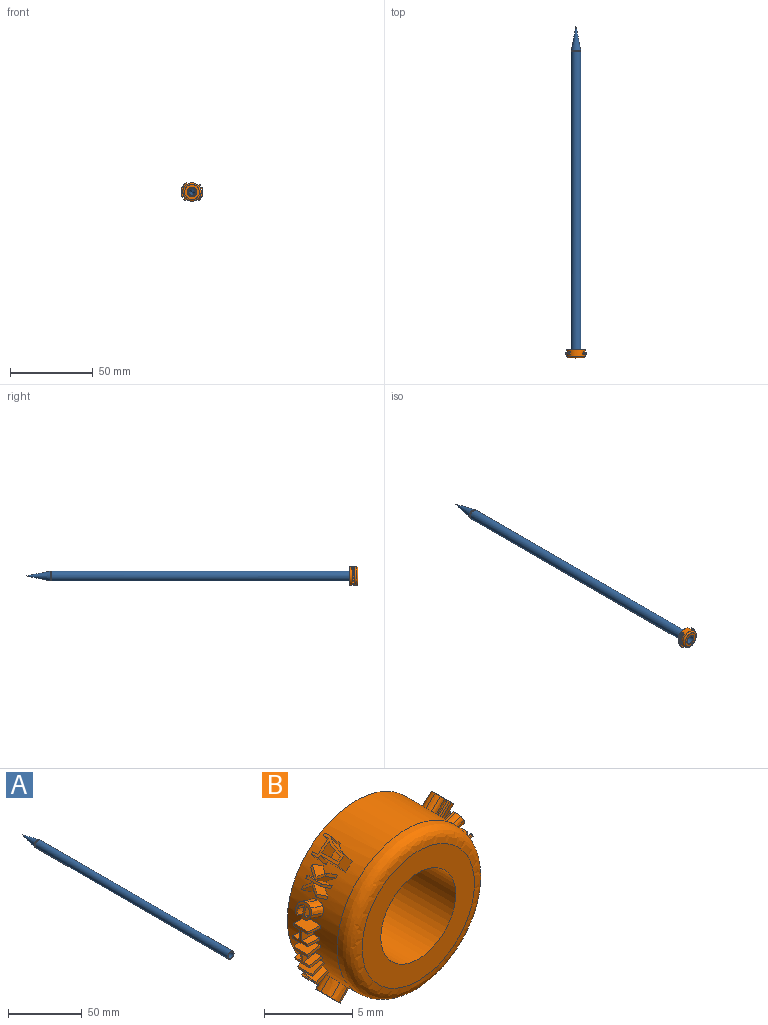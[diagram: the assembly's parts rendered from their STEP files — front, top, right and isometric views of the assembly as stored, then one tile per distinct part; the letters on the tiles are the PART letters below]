
ASSEMBLY  parts=2 mates=1
PART A: 8 faces, bbox 6x200x6 mm
  f0: cylinder r=2.5mm len=185mm, axis (0,1,0), area 2906mm2, adj f2,f4
  f1: cylinder r=3mm len=184.51mm, axis (0,1,0), area 3477.8mm2, adj f2,f5
  f2: plane 6x6mm, normal (0,-1,0), area 8.6mm2, adj f0,f1
  f3: cone r=3mm half-angle=11.3deg, axis (0,-1,0), area 135mm2, adj f5
  f4: plane 5x5mm, normal (0,-1,0), area 7.5mm2, adj f0,f6
  f5: revolved ~6x6mm, area 18.4mm2, adj f1,f3
  f6: revolved ~3.94x3.94mm, area 3.6mm2, adj f4,f7
  f7: cone r=2.02mm half-angle=11.3deg, axis (0,-1,0), area 59.2mm2, adj f6
PART B: 292 faces, bbox 13x5x11.3 mm
  f0: plane 1.56x0.74mm, normal (0.74,0,0.67), area 1.6mm2, adj f1,f9,f10,f32
  f1: plane 0.87x0.8mm, normal (0,-1,0), area 0.2mm2, adj f0,f2,f10,f32
  f2: plane 1.57x0.74mm, normal (-0.74,0,-0.67), area 1.6mm2, adj f1,f3,f10,f32
  f3: extruded ~0.78x0.71mm, area 0.2mm2, adj f2,f4,f10,f32
  f4: extruded ~0.86x0.79mm, area 0.2mm2, adj f3,f5,f10,f32
  f5: extruded ~0.86x0.79mm, area 0.2mm2, adj f4,f6,f10,f32
  f6: plane 0.75x0.67mm, normal (-0.74,0,-0.67), area 0.2mm2, adj f5,f7,f10,f32
  f7: extruded ~0.86x0.79mm, area 0.2mm2, adj f6,f8,f10,f32
  f8: extruded ~0.95x0.89mm, area 0.3mm2, adj f7,f9,f10,f32
  f9: extruded ~0.81x0.75mm, area 0.3mm2, adj f0,f8,f10,f32
  f10: cylinder r=6.5mm len=1.99mm, axis (0,1,0), area 0.4mm2, adj f0,f1,f2,f3,f4,f5,f6,f7
  f11: extruded ~0.92x0.75mm, area 0.2mm2, adj f12,f24,f30,f32
  f12: extruded ~0.93x0.77mm, area 0.2mm2, adj f11,f13,f30,f32
  f13: extruded ~1.06x0.94mm, area 0.5mm2, adj f12,f14,f30,f32
  f14: extruded ~0.9x0.73mm, area 0.5mm2, adj f13,f15,f30,f32
  f15: extruded ~0.89x0.72mm, area 0.5mm2, adj f14,f16,f30,f32
  f16: extruded ~1.04x0.91mm, area 0.4mm2, adj f15,f17,f30,f32
  f17: extruded ~1.02x0.89mm, area 0.4mm2, adj f16,f18,f30,f32
  f18: extruded ~0.89x0.71mm, area 0.4mm2, adj f17,f19,f30,f32
  f19: plane 0.8x0.6mm, normal (0.6,0,0.8), area 0.1mm2, adj f18,f20,f30,f32
  f20: plane 1.28x1.26mm, normal (0,1,0), area 0.8mm2, adj f19,f21,f30,f32
  f21: extruded ~0.87x0.69mm, area 0.3mm2, adj f20,f22,f30,f32
  f22: extruded ~0.97x0.83mm, area 0.3mm2, adj f21,f23,f30,f32
  f23: extruded ~1.04x0.91mm, area 0.4mm2, adj f22,f24,f30,f32
  f24: plane 0.8x0.6mm, normal (0.6,0,0.8), area 0.2mm2, adj f11,f23,f30,f32
  f25: plane 1.17x1.09mm, normal (0,-1,0), area 0.6mm2, adj f26,f29,f30,f31
  f26: extruded ~0.86x0.68mm, area 0.3mm2, adj f25,f27,f30,f31
  f27: extruded ~0.94x0.79mm, area 0.3mm2, adj f26,f28,f30,f31
  f28: extruded ~0.93x0.78mm, area 0.2mm2, adj f27,f29,f30,f31
  f29: extruded ~0.85x0.66mm, area 0.3mm2, adj f25,f28,f30,f31
  f30: cylinder r=6.5mm len=1.22mm, axis (0,1,0), area 0.5mm2, adj f11,f12,f13,f14,f15,f16,f17,f18
  f31: cylinder r=5.5mm len=0.49mm, axis (0,1,0), area 0.2mm2, adj f25,f26,f27,f28,f29
  f32: cylinder r=5.5mm len=11mm, axis (0,1,0), area 127.7mm2, adj f0,f1,f2,f3,f4,f5,f6,f7
  f33: plane 1.18x0.98mm, normal (0.21,0,-0.98), area 1.2mm2, adj f32,f34,f36,f37
  f34: plane 1.02x0.39mm, normal (0,1,0), area 0.2mm2, adj f32,f33,f35,f37
  f35: plane 1.18x0.98mm, normal (-0.21,0,0.98), area 1.2mm2, adj f32,f34,f36,f37
  f36: plane 1.02x0.39mm, normal (0,-1,0), area 0.2mm2, adj f32,f33,f35,f37
  f37: cylinder r=6.5mm len=1.18mm, axis (0,1,0), area 0.2mm2, adj f33,f34,f35,f36
  f38: extruded ~0.99x0.28mm, area 0.1mm2, adj f32,f39,f45,f46
  f39: extruded ~0.98x0.24mm, area 0.1mm2, adj f32,f38,f40,f46
  f40: extruded ~0.98x0.24mm, area 0.1mm2, adj f32,f39,f41,f46
  f41: extruded ~0.99x0.28mm, area 0.1mm2, adj f32,f40,f42,f46
  f42: extruded ~0.99x0.29mm, area 0.1mm2, adj f32,f41,f43,f46
  f43: extruded ~0.98x0.24mm, area 0.1mm2, adj f32,f42,f44,f46
  f44: extruded ~0.98x0.24mm, area 0.1mm2, adj f32,f43,f45,f46
  f45: extruded ~0.99x0.29mm, area 0.1mm2, adj f32,f38,f44,f46
  f46: cylinder r=6.5mm len=0.24mm, axis (0,1,0), area 0mm2, adj f38,f39,f40,f41,f42,f43,f44,f45
  f47: extruded ~1.01x0.54mm, area 0.2mm2, adj f32,f48,f60,f66
  f48: extruded ~1.01x0.56mm, area 0.2mm2, adj f32,f47,f49,f66
  f49: extruded ~1.09x0.76mm, area 0.5mm2, adj f32,f48,f50,f66
  f50: extruded ~1x0.51mm, area 0.5mm2, adj f32,f49,f51,f66
  f51: extruded ~0.99x0.5mm, area 0.5mm2, adj f32,f50,f52,f66
  f52: extruded ~1.08x0.72mm, area 0.4mm2, adj f32,f51,f53,f66
  f53: extruded ~1.07x0.7mm, area 0.4mm2, adj f32,f52,f54,f66
  f54: extruded ~0.99x0.49mm, area 0.4mm2, adj f32,f53,f55,f66
  f55: plane 0.93x0.37mm, normal (-0.37,0,0.93), area 0.1mm2, adj f32,f54,f56,f66
  f56: plane 1.24x1.12mm, normal (0,1,0), area 0.8mm2, adj f32,f55,f57,f66
  f57: extruded ~0.97x0.47mm, area 0.3mm2, adj f32,f56,f58,f66
  f58: extruded ~1.04x0.63mm, area 0.3mm2, adj f32,f57,f59,f66
  f59: extruded ~1.08x0.72mm, area 0.4mm2, adj f32,f58,f60,f66
  f60: plane 0.93x0.37mm, normal (-0.37,0,0.93), area 0.2mm2, adj f32,f47,f59,f66
  f61: plane 1.16x0.94mm, normal (0,-1,0), area 0.6mm2, adj f62,f65,f66,f67
  f62: extruded ~0.97x0.46mm, area 0.3mm2, adj f61,f63,f66,f67
  f63: extruded ~1.02x0.58mm, area 0.3mm2, adj f62,f64,f66,f67
  f64: extruded ~1.01x0.57mm, area 0.2mm2, adj f63,f65,f66,f67
  f65: extruded ~0.96x0.44mm, area 0.3mm2, adj f61,f64,f66,f67
  f66: cylinder r=6.5mm len=1.22mm, axis (0,1,0), area 0.5mm2, adj f47,f48,f49,f50,f51,f52,f53,f54
  f67: cylinder r=5.5mm len=0.57mm, axis (0,1,0), area 0.2mm2, adj f61,f62,f63,f64,f65
  f68: extruded ~1.01x0.97mm, area 0.4mm2, adj f32,f69,f82,f93
  f69: extruded ~0.84x0.79mm, area 0.5mm2, adj f32,f68,f70,f93
  f70: extruded ~0.87x0.82mm, area 0.7mm2, adj f32,f69,f71,f93
  f71: extruded ~1.1x1.08mm, area 0.6mm2, adj f32,f70,f72,f93
  f72: extruded ~0.87x0.83mm, area 0.2mm2, adj f32,f71,f73,f93
  f73: plane 0.74x0.68mm, normal (-0.68,0,0.73), area 0.2mm2, adj f32,f72,f74,f93
  f74: extruded ~0.87x0.83mm, area 0.2mm2, adj f32,f73,f75,f93
  f75: extruded ~1x0.96mm, area 0.4mm2, adj f32,f74,f76,f93
  f76: extruded ~0.84x0.79mm, area 0.5mm2, adj f32,f75,f77,f93
  f77: plane 0.74x0.69mm, normal (0,-1,0), area 0mm2, adj f32,f76,f78,f93
  f78: extruded ~1x0.96mm, area 0.4mm2, adj f32,f77,f79,f93
  f79: extruded ~0.97x0.93mm, area 0.4mm2, adj f32,f78,f80,f93
  f80: extruded ~0.83x0.78mm, area 0.4mm2, adj f32,f79,f81,f93
  f81: extruded ~0.83x0.79mm, area 0.4mm2, adj f32,f80,f82,f93
  f82: extruded ~0.99x0.95mm, area 0.4mm2, adj f32,f68,f81,f93
  f83: extruded ~0.77x0.71mm, area 0.2mm2, adj f84,f92,f93,f94
  f84: extruded ~0.77x0.72mm, area 0.2mm2, adj f83,f85,f93,f94
  f85: extruded ~0.83x0.78mm, area 0.2mm2, adj f84,f86,f93,f94
  f86: extruded ~0.86x0.81mm, area 0.2mm2, adj f85,f87,f93,f94
  f87: extruded ~0.9x0.86mm, area 0.3mm2, adj f86,f88,f93,f94
  f88: extruded ~0.79x0.74mm, area 0.3mm2, adj f87,f89,f93,f94
  f89: extruded ~0.8x0.75mm, area 0.3mm2, adj f88,f90,f93,f94
  f90: extruded ~0.9x0.86mm, area 0.3mm2, adj f89,f91,f93,f94
  f91: extruded ~0.86x0.81mm, area 0.2mm2, adj f90,f92,f93,f94
  f92: extruded ~0.82x0.77mm, area 0.2mm2, adj f83,f91,f93,f94
  f93: cylinder r=6.5mm len=1.62mm, axis (0,1,0), area 0.6mm2, adj f68,f69,f70,f71,f72,f73,f74,f75
  f94: cylinder r=5.5mm len=0.71mm, axis (0,1,0), area 0.4mm2, adj f83,f84,f85,f86,f87,f88,f89,f90
  f95: plane 0.92x0.78mm, normal (0,-1,0), area 0.2mm2, adj f32,f96,f107,f113
  f96: plane 0.78x0.64mm, normal (-0.77,0,-0.63), area 0.6mm2, adj f32,f95,f97,f113
  f97: plane 0.9x0.76mm, normal (0,1,0), area 0.2mm2, adj f32,f96,f98,f113
  f98: plane 0.78x0.63mm, normal (0.77,0,0.63), area 0.4mm2, adj f32,f97,f99,f113
  f99: plane 1.49x1.46mm, normal (0,1,0), area 1.1mm2, adj f32,f98,f100,f113
  f100: plane 0.78x0.64mm, normal (-0.77,0,-0.63), area 0.4mm2, adj f32,f99,f101,f113
  f101: plane 0.87x0.79mm, normal (0,1,0), area 0.2mm2, adj f32,f100,f102,f113
  f102: plane 0.78x0.64mm, normal (0.77,0,0.63), area 0.6mm2, adj f32,f101,f103,f113
  f103: plane 0.85x0.74mm, normal (0,-1,0), area 0.1mm2, adj f32,f102,f104,f113
  f104: extruded ~0.98x0.87mm, area 0.7mm2, adj f32,f103,f105,f113
  f105: extruded ~0.86x0.74mm, area 0.7mm2, adj f32,f104,f106,f113
  f106: plane 1.23x1.17mm, normal (0,-1,0), area 0.7mm2, adj f32,f105,f107,f113
  f107: plane 1.41x0.78mm, normal (-0.77,0,-0.63), area 1.4mm2, adj f32,f95,f106,f113
  f108: extruded ~0.86x0.74mm, area 0.6mm2, adj f109,f112,f113,f114
  f109: plane 1.01x0.91mm, normal (0,1,0), area 0.4mm2, adj f108,f110,f113,f114
  f110: plane 1.24x0.78mm, normal (0.77,0,0.63), area 1.2mm2, adj f109,f111,f113,f114
  f111: plane 1.24x1.22mm, normal (0,-1,0), area 0.7mm2, adj f110,f112,f113,f114
  f112: extruded ~0.95x0.84mm, area 0.7mm2, adj f108,f111,f113,f114
  f113: cylinder r=6.5mm len=1.98mm, axis (0,1,0), area 1mm2, adj f95,f96,f97,f98,f99,f100,f101,f102
  f114: cylinder r=5.5mm len=1.24mm, axis (0,1,0), area 0.6mm2, adj f108,f109,f110,f111,f112
  f115: plane 1.13x0.94mm, normal (-0.42,-0.65,-0.64), area 0.8mm2, adj f32,f116,f132,f133
  f116: plane 0.84x0.57mm, normal (0.55,0,0.84), area 0.6mm2, adj f32,f115,f117,f133
  f117: plane 0.93x0.69mm, normal (0,-1,0), area 0.2mm2, adj f32,f116,f118,f133
  f118: plane 0.84x0.57mm, normal (-0.55,0,-0.84), area 0.6mm2, adj f32,f117,f119,f133
  f119: plane 1.09x0.97mm, normal (0.42,-0.65,0.64), area 0.8mm2, adj f32,f118,f120,f133
  f120: plane 0.93x0.73mm, normal (0,-1,0), area 0.2mm2, adj f32,f119,f121,f133
  f121: plane 1.08x0.98mm, normal (-0.42,0.65,-0.63), area 0.8mm2, adj f32,f120,f122,f133
  f122: plane 1.1x1.02mm, normal (-0.41,-0.66,-0.63), area 0.8mm2, adj f32,f121,f123,f133
  f123: plane 0.94x0.74mm, normal (0,1,0), area 0.2mm2, adj f32,f122,f124,f133
  f124: plane 1.1x1mm, normal (0.41,0.66,0.63), area 0.8mm2, adj f32,f123,f125,f133
  f125: plane 0.84x0.6mm, normal (-0.55,0,-0.84), area 0.6mm2, adj f32,f124,f126,f133
  f126: plane 0.93x0.69mm, normal (0,1,0), area 0.2mm2, adj f32,f125,f127,f133
  f127: plane 0.84x0.6mm, normal (0.55,0,0.84), area 0.6mm2, adj f32,f126,f128,f133
  f128: plane 1.15x0.96mm, normal (-0.41,0.66,-0.63), area 0.8mm2, adj f32,f127,f129,f133
  f129: plane 0.98x0.71mm, normal (0,1,0), area 0.2mm2, adj f32,f128,f130,f133
  f130: plane 1.18x0.97mm, normal (0.41,-0.66,0.63), area 0.8mm2, adj f32,f129,f131,f133
  f131: plane 1.15x0.94mm, normal (0.42,0.65,0.63), area 0.8mm2, adj f32,f130,f132,f133
  f132: plane 0.97x0.7mm, normal (0,-1,0), area 0.2mm2, adj f32,f115,f131,f133
  f133: cylinder r=6.5mm len=1.34mm, axis (0,1,0), area 0.7mm2, adj f115,f116,f117,f118,f119,f120,f121,f122
  f134: extruded ~1.02x0.48mm, area 0.2mm2, adj f32,f135,f147,f153
  f135: extruded ~1.02x0.5mm, area 0.2mm2, adj f32,f134,f136,f153
  f136: extruded ~1.09x0.7mm, area 0.5mm2, adj f32,f135,f137,f153
  f137: extruded ~1.01x0.45mm, area 0.5mm2, adj f32,f136,f138,f153
  f138: extruded ~1.01x0.45mm, area 0.5mm2, adj f32,f137,f139,f153
  f139: extruded ~1.08x0.66mm, area 0.4mm2, adj f32,f138,f140,f153
  f140: extruded ~1.07x0.64mm, area 0.4mm2, adj f32,f139,f141,f153
  f141: extruded ~1x0.43mm, area 0.4mm2, adj f32,f140,f142,f153
  f142: plane 0.96x0.3mm, normal (-0.3,0,-0.95), area 0.1mm2, adj f32,f141,f143,f153
  f143: plane 1.19x1.08mm, normal (0,1,0), area 0.8mm2, adj f32,f142,f144,f153
  f144: extruded ~0.99x0.4mm, area 0.3mm2, adj f32,f143,f145,f153
  f145: extruded ~1.04x0.57mm, area 0.3mm2, adj f32,f144,f146,f153
  f146: extruded ~1.08x0.67mm, area 0.4mm2, adj f32,f145,f147,f153
  f147: plane 0.96x0.3mm, normal (-0.3,0,-0.95), area 0.2mm2, adj f32,f134,f146,f153
  f148: plane 1.14x0.89mm, normal (0,-1,0), area 0.6mm2, adj f149,f152,f153,f154
  f149: extruded ~0.99x0.4mm, area 0.3mm2, adj f148,f150,f153,f154
  f150: extruded ~1.03x0.52mm, area 0.3mm2, adj f149,f151,f153,f154
  f151: extruded ~1.02x0.51mm, area 0.2mm2, adj f150,f152,f153,f154
  f152: extruded ~0.98x0.37mm, area 0.3mm2, adj f148,f151,f153,f154
  f153: cylinder r=6.5mm len=1.22mm, axis (0,1,0), area 0.5mm2, adj f134,f135,f136,f137,f138,f139,f140,f141
  f154: cylinder r=5.5mm len=0.59mm, axis (0,1,0), area 0.2mm2, adj f148,f149,f150,f151,f152
  f155: extruded ~1x0.98mm, area 0.4mm2, adj f32,f156,f169,f180
  f156: extruded ~0.83x0.81mm, area 0.5mm2, adj f32,f155,f157,f180
  f157: extruded ~0.86x0.84mm, area 0.7mm2, adj f32,f156,f158,f180
  f158: extruded ~1.09x1.08mm, area 0.6mm2, adj f32,f157,f159,f180
  f159: extruded ~0.86x0.84mm, area 0.2mm2, adj f32,f158,f160,f180
  f160: plane 0.72x0.7mm, normal (0.72,0,-0.7), area 0.2mm2, adj f32,f159,f161,f180
  f161: extruded ~0.86x0.84mm, area 0.2mm2, adj f32,f160,f162,f180
  f162: extruded ~0.99x0.97mm, area 0.4mm2, adj f32,f161,f163,f180
  f163: extruded ~0.83x0.81mm, area 0.5mm2, adj f32,f162,f164,f180
  f164: plane 0.73x0.71mm, normal (0,-1,0), area 0mm2, adj f32,f163,f165,f180
  f165: extruded ~0.99x0.97mm, area 0.4mm2, adj f32,f164,f166,f180
  f166: extruded ~0.96x0.95mm, area 0.4mm2, adj f32,f165,f167,f180
  f167: extruded ~0.81x0.79mm, area 0.4mm2, adj f32,f166,f168,f180
  f168: extruded ~0.82x0.8mm, area 0.4mm2, adj f32,f167,f169,f180
  f169: extruded ~0.98x0.96mm, area 0.4mm2, adj f32,f155,f168,f180
  f170: extruded ~0.75x0.73mm, area 0.2mm2, adj f171,f179,f180,f181
  f171: extruded ~0.75x0.73mm, area 0.2mm2, adj f170,f172,f180,f181
  f172: extruded ~0.81x0.79mm, area 0.2mm2, adj f171,f173,f180,f181
  f173: extruded ~0.84x0.83mm, area 0.2mm2, adj f172,f174,f180,f181
  f174: extruded ~0.89x0.87mm, area 0.3mm2, adj f173,f175,f180,f181
  f175: extruded ~0.78x0.76mm, area 0.3mm2, adj f174,f176,f180,f181
  f176: extruded ~0.78x0.76mm, area 0.3mm2, adj f175,f177,f180,f181
  f177: extruded ~0.89x0.87mm, area 0.3mm2, adj f176,f178,f180,f181
  f178: extruded ~0.85x0.83mm, area 0.2mm2, adj f177,f179,f180,f181
  f179: extruded ~0.81x0.79mm, area 0.2mm2, adj f170,f178,f180,f181
  f180: cylinder r=6.5mm len=1.62mm, axis (0,1,0), area 0.6mm2, adj f155,f156,f157,f158,f159,f160,f161,f162
  f181: cylinder r=5.5mm len=0.71mm, axis (0,1,0), area 0.4mm2, adj f170,f171,f172,f173,f174,f175,f176,f177
  f182: plane 0.92x0.8mm, normal (0.41,0,0.91), area 0.8mm2, adj f32,f183,f200,f209
  f183: plane 0.96x0.54mm, normal (0,1,0), area 0.1mm2, adj f32,f182,f184,f209
  f184: plane 0.93x0.44mm, normal (-0.4,0.21,-0.89), area 0.2mm2, adj f32,f183,f185,f209
  f185: plane 0.92x0.42mm, normal (0,1,0), area 0mm2, adj f32,f184,f186,f209
  f186: extruded ~0.99x0.57mm, area 0.2mm2, adj f32,f185,f187,f209
  f187: extruded ~1x0.61mm, area 0.2mm2, adj f32,f186,f188,f209
  f188: extruded ~1.04x0.67mm, area 0.3mm2, adj f32,f187,f189,f209
  f189: extruded ~0.96x0.5mm, area 0.3mm2, adj f32,f188,f190,f209
  f190: extruded ~1.17x0.94mm, area 0.8mm2, adj f32,f189,f191,f209
  f191: plane 0.99x0.6mm, normal (-0.01,-1,-0.03), area 0.2mm2, adj f32,f190,f192,f209
  f192: plane 0.91x0.41mm, normal (-0.41,0,-0.91), area 0.1mm2, adj f32,f191,f193,f209
  f193: extruded ~0.94x0.47mm, area 0.2mm2, adj f32,f192,f194,f209
  f194: extruded ~0.99x0.59mm, area 0.2mm2, adj f32,f193,f195,f209
  f195: extruded ~1.06x0.72mm, area 0.3mm2, adj f32,f194,f196,f209
  f196: plane 0.94x0.46mm, normal (-0.38,0.37,-0.85), area 0.1mm2, adj f32,f195,f197,f209
  f197: extruded ~1x0.59mm, area 0.2mm2, adj f32,f196,f198,f209
  f198: extruded ~1x0.6mm, area 0.2mm2, adj f32,f197,f199,f209
  f199: extruded ~1.05x0.7mm, area 0.3mm2, adj f32,f198,f200,f209
  f200: extruded ~0.96x0.51mm, area 0.3mm2, adj f32,f182,f199,f209
  f201: extruded ~0.94x0.46mm, area 0.2mm2, adj f202,f208,f209,f210
  f202: extruded ~0.98x0.56mm, area 0.2mm2, adj f201,f203,f209,f210
  f203: extruded ~1.02x0.65mm, area 0.3mm2, adj f202,f204,f209,f210
  f204: extruded ~0.96x0.5mm, area 0.3mm2, adj f203,f205,f209,f210
  f205: plane 0.91x0.41mm, normal (-0.41,0,-0.91), area 0.1mm2, adj f204,f206,f209,f210
  f206: plane 0.98x0.58mm, normal (0.02,1,0.04), area 0.2mm2, adj f205,f207,f209,f210
  f207: extruded ~1.04x0.69mm, area 0.3mm2, adj f206,f208,f209,f210
  f208: extruded ~0.96x0.5mm, area 0.2mm2, adj f201,f207,f209,f210
  f209: cylinder r=6.5mm len=1.22mm, axis (0,1,0), area 0.5mm2, adj f182,f183,f184,f185,f186,f187,f188,f189
  f210: cylinder r=5.5mm len=0.53mm, axis (0,1,0), area 0.2mm2, adj f201,f202,f203,f204,f205,f206,f207,f208
  f211: plane 1x0.77mm, normal (-0.05,0,1), area 0.8mm2, adj f32,f212,f226,f228
  f212: plane 1.02x0.22mm, normal (0,1,0), area 0.2mm2, adj f32,f211,f213,f228
  f213: plane 1x0.76mm, normal (0.05,0,-1), area 0.8mm2, adj f32,f212,f214,f228
  f214: extruded ~1.01x0.22mm, area 0.2mm2, adj f32,f213,f215,f228
  f215: extruded ~1.01x0.25mm, area 0.2mm2, adj f32,f214,f216,f228
  f216: extruded ~1.01x0.32mm, area 0.3mm2, adj f32,f215,f217,f228
  f217: extruded ~1.01x0.33mm, area 0.3mm2, adj f32,f216,f218,f228
  f218: plane 1x0.62mm, normal (-0.05,0,1), area 0.6mm2, adj f32,f217,f227,f228
  f219: plane 1.18x1mm, normal (0.05,0,-1), area 1.2mm2, adj f32,f220,f227,f228
  f220: plane 1x0.19mm, normal (0,-1,0), area 0.1mm2, adj f32,f219,f221,f228
  f221: plane 1x0.16mm, normal (-0.04,-0.18,0.98), area 0.2mm2, adj f32,f220,f222,f228
  f222: plane 1x0.05mm, normal (0,-1,0), area 0mm2, adj f32,f221,f223,f228
  f223: extruded ~1.01x0.2mm, area 0.2mm2, adj f32,f222,f224,f228
  f224: extruded ~1.01x0.27mm, area 0.2mm2, adj f32,f223,f225,f228
  f225: extruded ~1.03x0.37mm, area 0.3mm2, adj f32,f224,f226,f228
  f226: extruded ~1.02x0.33mm, area 0.4mm2, adj f32,f211,f225,f228
  f227: plane 1x0.22mm, normal (0,1,0), area 0.2mm2, adj f32,f218,f219,f228
  f228: cylinder r=6.5mm len=1.2mm, axis (0,1,0), area 0.5mm2, adj f211,f212,f213,f214,f215,f216,f217,f218
  f229: plane 0.99x0.77mm, normal (0.19,0,0.98), area 0.8mm2, adj f32,f230,f244,f246
  f230: plane 1.01x0.37mm, normal (0,1,0), area 0.2mm2, adj f32,f229,f231,f246
  f231: plane 0.98x0.76mm, normal (-0.19,0,-0.98), area 0.8mm2, adj f32,f230,f232,f246
  f232: extruded ~1x0.26mm, area 0.2mm2, adj f32,f231,f233,f246
  f233: extruded ~1.03x0.4mm, area 0.2mm2, adj f32,f232,f234,f246
  f234: extruded ~1.04x0.46mm, area 0.3mm2, adj f32,f233,f235,f246
  f235: extruded ~1x0.33mm, area 0.3mm2, adj f32,f234,f236,f246
  f236: plane 0.98x0.62mm, normal (0.19,0,0.98), area 0.6mm2, adj f32,f235,f245,f246
  f237: plane 1.18x0.98mm, normal (-0.19,0,-0.98), area 1.2mm2, adj f32,f238,f245,f246
  f238: plane 1.02x0.33mm, normal (0,-1,0), area 0.1mm2, adj f32,f237,f239,f246
  f239: plane 0.99x0.22mm, normal (0.19,-0.18,0.97), area 0.2mm2, adj f32,f238,f240,f246
  f240: plane 0.98x0.2mm, normal (0,-1,0), area 0mm2, adj f32,f239,f241,f246
  f241: extruded ~1.02x0.35mm, area 0.2mm2, adj f32,f240,f242,f246
  f242: extruded ~1.03x0.41mm, area 0.2mm2, adj f32,f241,f243,f246
  f243: extruded ~1.06x0.51mm, area 0.3mm2, adj f32,f242,f244,f246
  f244: extruded ~1.01x0.33mm, area 0.4mm2, adj f32,f229,f243,f246
  f245: plane 1.03x0.37mm, normal (0,1,0), area 0.2mm2, adj f32,f236,f237,f246
  f246: cylinder r=6.5mm len=1.2mm, axis (0,1,0), area 0.5mm2, adj f229,f230,f231,f232,f233,f234,f235,f236
  f247: plane 1.18x1mm, normal (0.07,0,1), area 1.2mm2, adj f32,f248,f258,f259
  f248: plane 1.02x0.25mm, normal (0,-1,0), area 0.2mm2, adj f32,f247,f249,f259
  f249: plane 1x0.49mm, normal (-0.07,0,-1), area 0.5mm2, adj f32,f248,f250,f259
  f250: plane 1.04x0.73mm, normal (0,-1,0), area 0.7mm2, adj f32,f249,f251,f259
  f251: plane 1x0.49mm, normal (0.07,0,1), area 0.5mm2, adj f32,f250,f252,f259
  f252: plane 1x0.25mm, normal (0,-1,0), area 0.2mm2, adj f32,f251,f253,f259
  f253: plane 1.18x1mm, normal (-0.07,0,-1), area 1.2mm2, adj f32,f252,f254,f259
  f254: plane 1x0.25mm, normal (0,1,0), area 0.2mm2, adj f32,f253,f255,f259
  f255: plane 1x0.53mm, normal (0.07,0,1), area 0.5mm2, adj f32,f254,f256,f259
  f256: plane 1.04x0.73mm, normal (0,1,0), area 0.7mm2, adj f32,f255,f257,f259
  f257: plane 1x0.53mm, normal (-0.07,0,-1), area 0.5mm2, adj f32,f256,f258,f259
  f258: plane 1.02x0.25mm, normal (0,1,0), area 0.2mm2, adj f32,f247,f257,f259
  f259: cylinder r=6.5mm len=1.18mm, axis (0,1,0), area 0.5mm2, adj f247,f248,f249,f250,f251,f252,f253,f254
  f260: plane 0.91x0.75mm, normal (0.41,0,-0.91), area 0.7mm2, adj f32,f261,f272,f274
  f261: plane 0.92x0.42mm, normal (0.41,0.04,-0.91), area 0.2mm2, adj f32,f260,f262,f274
  f262: plane 0.91x0.41mm, normal (0.41,0.06,-0.91), area 0.1mm2, adj f32,f261,f263,f274
  f263: plane 1.17x1mm, normal (-0.35,-0.54,0.77), area 1.2mm2, adj f32,f262,f264,f274
  f264: plane 1.02x0.61mm, normal (0,-1,0), area 0.2mm2, adj f32,f263,f265,f274
  f265: plane 1.18x0.92mm, normal (0.41,0,-0.91), area 1.2mm2, adj f32,f264,f266,f274
  f266: plane 0.99x0.56mm, normal (0,1,0), area 0.2mm2, adj f32,f265,f267,f274
  f267: plane 0.91x0.72mm, normal (-0.41,0,0.91), area 0.7mm2, adj f32,f266,f268,f274
  f268: plane 0.92x0.41mm, normal (-0.41,-0.02,0.91), area 0.1mm2, adj f32,f267,f269,f274
  f269: plane 0.92x0.42mm, normal (-0.41,-0.04,0.91), area 0.1mm2, adj f32,f268,f270,f274
  f270: plane 1.18x1mm, normal (0.35,0.54,-0.77), area 1.2mm2, adj f32,f269,f273,f274
  f271: plane 1.18x0.92mm, normal (-0.41,0,0.91), area 1.2mm2, adj f32,f272,f273,f274
  f272: plane 0.97x0.57mm, normal (0,-1,0), area 0.2mm2, adj f32,f260,f271,f274
  f273: plane 0.99x0.62mm, normal (0,1,0), area 0.2mm2, adj f32,f270,f271,f274
  f274: cylinder r=6.5mm len=1.18mm, axis (0,1,0), area 0.6mm2, adj f260,f261,f262,f263,f264,f265,f266,f267
  f275: plane 0.99x0.49mm, normal (0.18,0,-0.98), area 0.5mm2, adj f32,f276,f285,f287
  f276: plane 1.11x0.83mm, normal (0,-1,0), area 0.7mm2, adj f32,f275,f277,f287
  f277: plane 0.99x0.49mm, normal (-0.18,0,0.98), area 0.5mm2, adj f32,f276,f278,f287
  f278: plane 1.03x0.35mm, normal (0,-1,0), area 0.2mm2, adj f32,f277,f279,f287
  f279: plane 1.18x0.99mm, normal (0.18,0,-0.98), area 1.2mm2, adj f32,f278,f280,f287
  f280: plane 1.03x0.35mm, normal (0,1,0), area 0.2mm2, adj f32,f279,f281,f287
  f281: plane 0.99x0.53mm, normal (-0.18,0,0.98), area 0.5mm2, adj f32,f280,f282,f287
  f282: plane 1.11x0.83mm, normal (0,1,0), area 0.7mm2, adj f32,f281,f283,f287
  f283: plane 0.99x0.53mm, normal (0.18,0,-0.98), area 0.5mm2, adj f32,f282,f286,f287
  f284: plane 1.18x0.99mm, normal (-0.18,0,0.98), area 1.2mm2, adj f32,f285,f286,f287
  f285: plane 1.01x0.35mm, normal (0,-1,0), area 0.2mm2, adj f32,f275,f284,f287
  f286: plane 1.01x0.35mm, normal (0,1,0), area 0.2mm2, adj f32,f283,f284,f287
  f287: cylinder r=6.5mm len=1.18mm, axis (0,1,0), area 0.5mm2, adj f275,f276,f277,f278,f279,f280,f281,f282
  f288: plane 9.01x9.01mm, normal (0,-1,0), area 35.3mm2, adj f290,f291
  f289: plane 11x11mm, normal (0,1,0), area 66.8mm2, adj f32,f290
  f290: cylinder r=3mm len=6mm, axis (0,1,0), area 94.2mm2, adj f288,f289
  f291: bspline ~11.29x11.29mm, area 52.7mm2, adj f32,f288
PLACE A t=(1.43,82.04,-4.39)mm
PLACE B t=(1.43,-97.96,-4.39)mm
MATE fastened B.f290 <-> A.f1  axis (0,-1,0) through (1.43,-102.96,-4.39)mm
